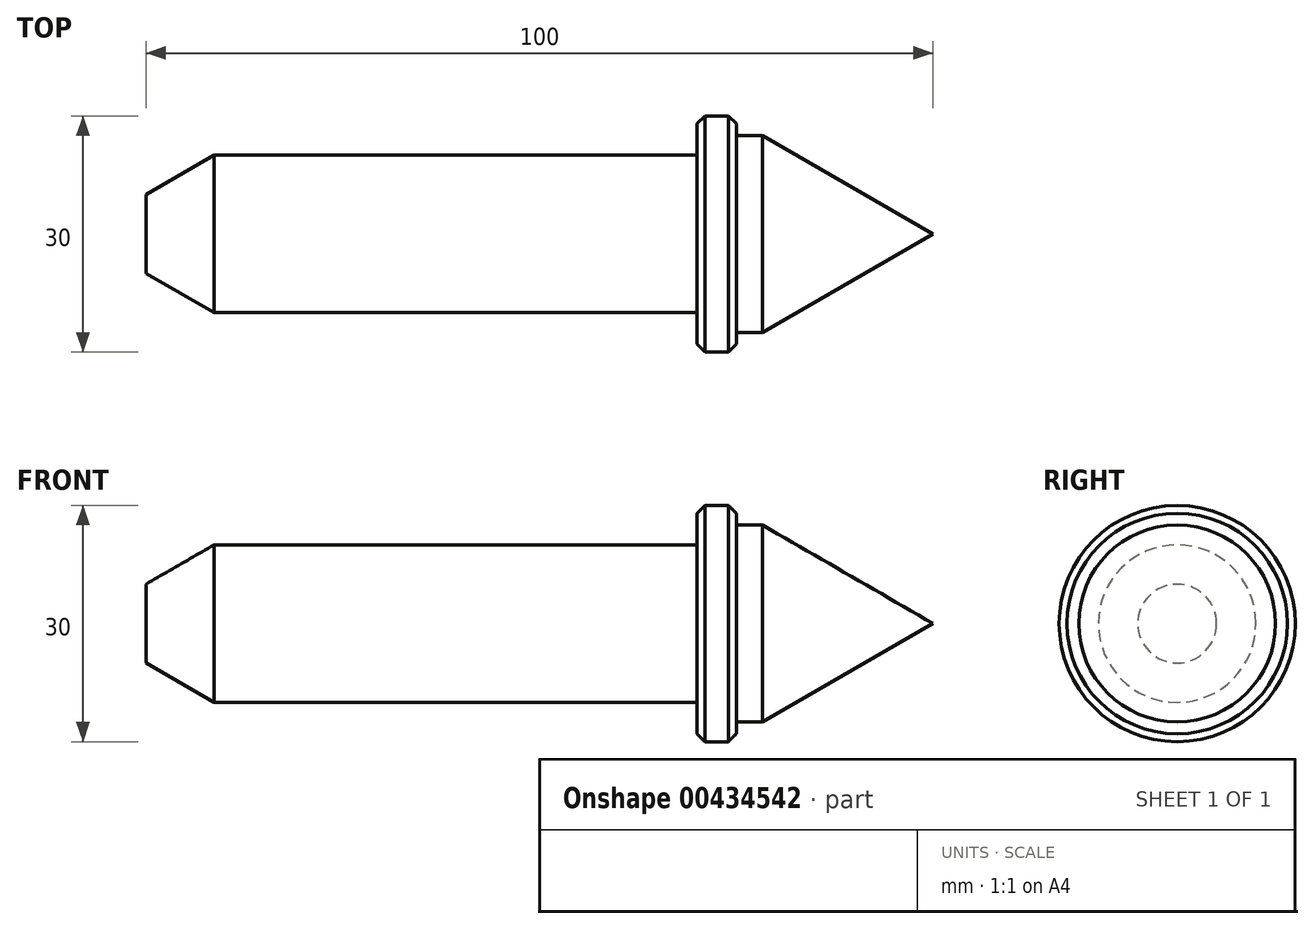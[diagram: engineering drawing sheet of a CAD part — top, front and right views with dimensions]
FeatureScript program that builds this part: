
annotation { "Feature Type Name" : "Feature", "Feature Type Description" : "" }
export const myFeature = defineFeature(function(context is Context, id is Id, definition is map)
    precondition{}
    {
        {
            var Q0;
            Q0=qCreatedBy(makeId("Front.planeOp"),FACE);
            var sketch = newSketch(context, id + "F0", { "sketchPlane" : qUnion([Q0])});
            skLineSegment(sketch, "E0", {"start": v(28.72, 10) * mm, "end": v(28.72, 0) * mm});
            skLineSegment(sketch, "E1", {"start": v(28.72, 0) * mm, "end": v(128.72, 0) * mm});
            skLineSegment(sketch, "E2", {"start": v(28.72, 10) * mm, "end": v(98.72, 10) * mm});
            skLineSegment(sketch, "E3", {"start": v(98.72, 10) * mm, "end": v(98.72, 15) * mm});
            skLineSegment(sketch, "E4", {"start": v(98.72, 15) * mm, "end": v(103.72, 15) * mm});
            skLineSegment(sketch, "E5", {"start": v(103.72, 15) * mm, "end": v(103.72, 12.5) * mm});
            skLineSegment(sketch, "E6", {"start": v(103.72, 12.5) * mm, "end": v(107.06, 12.5) * mm});
            skLineSegment(sketch, "E7", {"start": v(107.06, 12.5) * mm, "end": v(128.72, 0) * mm});
            skLineSegment(sketch, "E8", {"start": v(153.76, 12.5) * mm, "end": v(153.76, -12.5) * mm});
            skPoint(sketch, "E9", {"position": v(153.76, 0) * mm});
            skLineSegment(sketch, "E10", {"start": v(28.72, 5) * mm, "end": v(37.38, 10) * mm});
            skSolve(sketch);
        }
        {
            var Q0;
            {var subQ3=sQuery(id+"F0.wireOp",EDGE,"E1");Q0=makeQuery(id+"F0.imprint","IMPRINT",FACE,{"disambiguationData":[TD([[makeQuery(id+"F0.imprint","IMPRINT",EDGE,{"derivedFrom":subQ3}),1.0]])]});}
            var Q1;
            Q1=sQuery(id+"F0.wireOp",EDGE,"E1");
            revolve(context, id + "F1", {"entities" : qUnion([Q0]), "axis" : qUnion([Q1]), "revolveType" : RevolveType.FULL});
        }
        {
            var Q0;
            Q0=makeQuery(id+"F1.opRevolve","SWEPT_EDGE",EDGE,{"disambiguationData":[OSD([sQuery(id+"F0.wireOp",EDGE,"E4"),sQuery(id+"F0.wireOp",EDGE,"E5")])]});
            var Q1;
            Q1=makeQuery(id+"F1.opRevolve","SWEPT_EDGE",EDGE,{"disambiguationData":[OSD([sQuery(id+"F0.wireOp",EDGE,"E3"),sQuery(id+"F0.wireOp",EDGE,"E4")])]});
            chamfer(context, id + "F2", {"entities" : qUnion([Q0, Q1]), "width" : 1 * mm, "tangentPropagation" : true});
        }
    });
